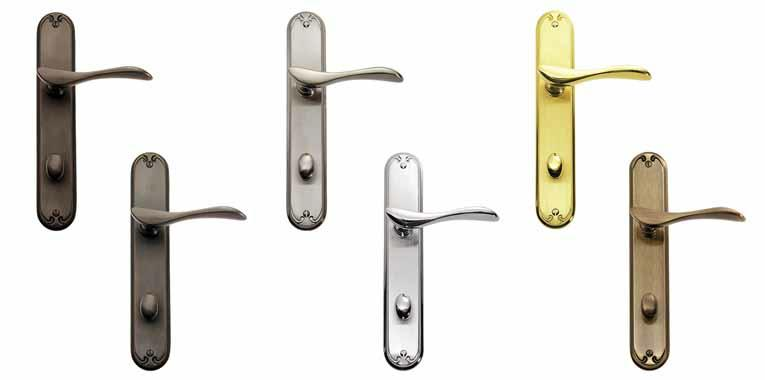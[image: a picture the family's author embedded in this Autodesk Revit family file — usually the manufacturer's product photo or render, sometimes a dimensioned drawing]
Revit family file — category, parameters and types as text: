
# Revit family: Door-French-Pella-Architect_Series-Hinged_Patio_Door-OutSwing-Active_Passive
name_source: partatom
category: Doors
revit_build: Autodesk Revit Architecture 2013 (Build: 20130531_2115(x64)
units: mm (PartAtom-declared; Revit-internal decimal feet)

## types (30) — shared parameters
Analytic Construction = <None>
Architectural Design Manual = www.pellaadm.com
Construction Type = -
Cross Grille Pattern = No
Custom Grille Pattern = No
Custom Horizontal Lites = 2
Custom Vertical Lites = 6
Description = Out-Swing French - Active / Passive Operation
Door Grille Visibility = Yes
Door Handle Height = 3' - 0"
Energy Efficiency = http://www.pella.com
Environmental Commitment = http://www.pella.com
Ext Finish = Aluminum - Pella - Brown
Function = Interior
Glazing Finish = Glass - Pella - Clear Insulating Glass
Glazing Thickness = 107/128"
Int Finish = Wood - Pella - Pine
Manufacturer = Pella - Windows & Doors
Note* = Maximum Frame Depth is 211 mm; if Wall Depth exceeds this value please recalculated Set Back to reflect
Operation = Hinged Patio Door
Prairie Grille Pattern = No
Product Documentation Link = http://media.pella.com
Product Name = Architect Series Hinged Patio Door
Product Page URL = http://www.pella.com
Series = Architect Series - Aluminum-Clad Wood
Thickness = 0"
Top Row Grille Pattern = No
Traditional Grille Pattern = Yes
URL = www.pella.com
Wall Closure = By host

## per-type parameters (varying)
| type | C Height | C Width | DLO Height | DLO Width | Height | Hinges | Rough Height | Rough Width | Unit Height | Unit Width | Width |
| 5080 | 6' - 7 1/2" | 4' - 2" | 5' - 5 63/128" | 1' - 0 13/16" | 6' - 7 1/2" | 3 | 6' - 8" | 4' - 2 3/4" | 6' - 5 3/8" | 1' - 11 23/256" | 4' - 2" |
| 5081 | 6' - 8" | 4' - 2" | 5' - 5 127/128" | 1' - 0 13/16" | 6' - 8" | 3 | 6' - 8 1/2" | 4' - 2 3/4" | 6' - 5 7/8" | 1' - 11 23/256" | 4' - 2" |
| 5082 | 6' - 10" | 4' - 2" | 5' - 7 127/128" | 1' - 0 13/16" | 6' - 10" | 3 | 6' - 10 1/2" | 4' - 2 3/4" | 6' - 7 7/8" | 1' - 11 23/256" | 4' - 2" |
| 5086 | 7' - 2" | 4' - 2" | 5' - 11 127/128" | 1' - 0 13/16" | 7' - 2" | 4 | 7' - 2 1/2" | 4' - 2 3/4" | 6' - 11 7/8" | 1' - 11 23/256" | 4' - 2" |
| 5096 | 7' - 11 1/2" | 4' - 2" | 6' - 9 63/128" | 1' - 0 13/16" | 7' - 11 1/2" | 4 | 8' - 0" | 4' - 2 3/4" | 7' - 9 3/8" | 1' - 11 23/256" | 4' - 2" |
| 50120 | 9' - 11 1/2" | 4' - 2" | 8' - 9 63/128" | 1' - 0 13/16" | 9' - 11 1/2" | 4 | 10' - 0" | 4' - 2 3/4" | 9' - 9 3/8" | 1' - 11 23/256" | 4' - 2" |
| 6080 | 6' - 7 1/2" | 4' - 11 1/4" | 5' - 5 63/128" | 1' - 5 7/16" | 6' - 7 1/2" | 3 | 6' - 8" | 5' - 0" | 6' - 5 3/8" | 2' - 3 183/256" | 4' - 11 1/4" |
| 6081 | 6' - 8" | 4' - 11 1/4" | 5' - 5 127/128" | 1' - 5 7/16" | 6' - 8" | 3 | 6' - 8 1/2" | 5' - 0" | 6' - 5 7/8" | 2' - 3 183/256" | 4' - 11 1/4" |
| 6082 | 6' - 10" | 4' - 11 1/4" | 5' - 7 127/128" | 1' - 5 7/16" | 6' - 10" | 3 | 6' - 10 1/2" | 5' - 0" | 6' - 7 7/8" | 2' - 3 183/256" | 4' - 11 1/4" |
| 6086 | 7' - 2" | 4' - 11 1/4" | 5' - 11 127/128" | 1' - 5 7/16" | 7' - 2" | 4 | 7' - 2 1/2" | 5' - 0" | 6' - 11 7/8" | 2' - 3 183/256" | 4' - 11 1/4" |
| 6096 | 7' - 11 1/2" | 4' - 11 1/4" | 6' - 9 63/128" | 1' - 5 7/16" | 7' - 11 1/2" | 4 | 8' - 0" | 5' - 0" | 7' - 9 3/8" | 2' - 3 183/256" | 4' - 11 1/4" |
| 60120 | 9' - 11 1/2" | 4' - 11 1/4" | 8' - 9 63/128" | 1' - 5 7/16" | 9' - 11 1/2" | 4 | 10' - 0" | 5' - 0" | 9' - 9 3/8" | 2' - 3 183/256" | 4' - 11 1/4" |
| 6780 | 6' - 7 1/2" | 5' - 6 1/4" | 5' - 5 63/128" | 1' - 8 15/16" | 6' - 7 1/2" | 3 | 6' - 8" | 5' - 7" | 6' - 5 3/8" | 2' - 7 55/256" | 5' - 6 1/4" |
| 6781 | 6' - 8" | 5' - 6 1/4" | 5' - 5 127/128" | 1' - 8 15/16" | 6' - 8" | 3 | 6' - 8 1/2" | 5' - 7" | 6' - 5 7/8" | 2' - 7 55/256" | 5' - 6 1/4" |
| 6782 | 6' - 10" | 5' - 6 1/4" | 5' - 7 127/128" | 1' - 8 15/16" | 6' - 10" | 3 | 6' - 10 1/2" | 5' - 7" | 6' - 7 7/8" | 2' - 7 55/256" | 5' - 6 1/4" |
| 6786 | 7' - 2" | 5' - 6 1/4" | 5' - 11 127/128" | 1' - 8 15/16" | 7' - 2" | 4 | 7' - 2 1/2" | 5' - 7" | 6' - 11 7/8" | 2' - 7 55/256" | 5' - 6 1/4" |
| 6796 | 7' - 11 1/2" | 5' - 6 1/4" | 6' - 9 63/128" | 1' - 8 15/16" | 7' - 11 1/2" | 4 | 8' - 0" | 5' - 7" | 7' - 9 3/8" | 2' - 7 55/256" | 5' - 6 1/4" |
| 67120 | 9' - 11 1/2" | 5' - 6 1/4" | 8' - 9 63/128" | 1' - 8 15/16" | 9' - 11 1/2" | 4 | 10' - 0" | 5' - 7" | 9' - 9 3/8" | 2' - 7 55/256" | 5' - 6 1/4" |
| 7280 | 6' - 7 1/2" | 5' - 11 1/4" | 5' - 5 63/128" | 1' - 11 7/16" | 6' - 7 1/2" | 3 | 6' - 8" | 6' - 0" | 6' - 5 3/8" | 2' - 9 183/256" | 5' - 11 1/4" |
| 7281 | 6' - 8" | 5' - 11 1/4" | 5' - 5 127/128" | 1' - 11 7/16" | 6' - 8" | 3 | 6' - 8 1/2" | 6' - 0" | 6' - 5 7/8" | 2' - 9 183/256" | 5' - 11 1/4" |
| 7282 | 6' - 10" | 5' - 11 1/4" | 5' - 7 127/128" | 1' - 11 7/16" | 6' - 10" | 3 | 6' - 10 1/2" | 6' - 0" | 6' - 7 7/8" | 2' - 9 183/256" | 5' - 11 1/4" |
| 7286 | 7' - 2" | 5' - 11 1/4" | 5' - 11 127/128" | 1' - 11 7/16" | 7' - 2" | 4 | 7' - 2 1/2" | 6' - 0" | 6' - 11 7/8" | 2' - 9 183/256" | 5' - 11 1/4" |
| 7296 | 7' - 11 1/2" | 5' - 11 1/4" | 6' - 9 63/128" | 1' - 11 7/16" | 7' - 11 1/2" | 4 | 8' - 0" | 6' - 0" | 7' - 9 3/8" | 2' - 9 183/256" | 5' - 11 1/4" |
| 72120 | 9' - 11 1/2" | 5' - 11 1/4" | 8' - 9 63/128" | 1' - 11 7/16" | 9' - 11 1/2" | 4 | 10' - 0" | 6' - 0" | 9' - 9 3/8" | 2' - 9 183/256" | 5' - 11 1/4" |
| 7580 | 6' - 7 1/2" | 6' - 3" | 5' - 5 63/128" | 2' - 1 5/16" | 6' - 7 1/2" | 3 | 6' - 8" | 6' - 3 3/4" | 6' - 5 3/8" | 2' - 11 151/256" | 6' - 3" |
| 7581 | 6' - 8" | 6' - 3" | 5' - 5 127/128" | 2' - 1 5/16" | 6' - 8" | 3 | 6' - 8 1/2" | 6' - 3 3/4" | 6' - 5 7/8" | 2' - 11 151/256" | 6' - 3" |
| 7582 | 6' - 10" | 6' - 3" | 5' - 7 127/128" | 2' - 1 5/16" | 6' - 10" | 3 | 6' - 10 1/2" | 6' - 3 3/4" | 6' - 7 7/8" | 2' - 11 151/256" | 6' - 3" |
| 7586 | 7' - 2" | 6' - 3" | 5' - 11 127/128" | 2' - 1 5/16" | 7' - 2" | 4 | 7' - 2 1/2" | 6' - 3 3/4" | 6' - 11 7/8" | 2' - 11 151/256" | 6' - 3" |
| 7596 | 7' - 11 1/2" | 6' - 3" | 6' - 9 63/128" | 2' - 1 5/16" | 7' - 11 1/2" | 4 | 8' - 0" | 6' - 3 3/4" | 7' - 9 3/8" | 2' - 11 151/256" | 6' - 3" |
| 75120 | 9' - 11 1/2" | 6' - 3" | 8' - 9 63/128" | 2' - 1 5/16" | 9' - 11 1/2" | 4 | 10' - 0" | 6' - 3 3/4" | 9' - 9 3/8" | 2' - 11 151/256" | 6' - 3" |

note: column(s) folded — value = type name in every type: Model

## geometry (parser evidence)
native form markers: Blend x6, Sweep x10
no freeform markers — native parametric forms only
